# Revit family: 30008 Трибуна двухрядная на 50 мест «Дабл-50» Хоббика
name_source: partatom
category: Антураж
revit_build: Autodesk Revit 2018 (Build: 20180423_1000(x64)
units: mm (PartAtom-declared; Revit-internal decimal feet)

## family parameters
Всегда вертикально = Да
Источник визуального образа = Геометрия семейства
На основе рабочей плоскости = Нет
Общий = Нет
При загрузке вырезать с полостями = Нет
Точка расчета площади = Нет

## types (1)
- Трибуна двухрядная на 50 мест «Дабл-50»
    URL = https://hobbyka.ru
    Артикул товара = Арт 30008
    Высота = 1500 мм
    Группа модели = Мобильные и стационарные трибуны
    Длина = 15400 мм
    Изготовитель = ООО «Хоббика»
    Изображение типоразмера = Трибуна двухрядная на 50 мест «Дабл-50» Арт 30008.jpg
    Материал изделия = Сталь, фанера, пластик
    Описание = Трибуна двухрядная на 50 мест «Дабл-50»
    Цвет каркаса = Сталь
    Цвет настила = Настил
    Цвет сидений = Красный
    Ширина = 1400 мм

## geometry (parser evidence)
native form markers: Blend x420, Sweep x1
no freeform markers — native parametric forms only
